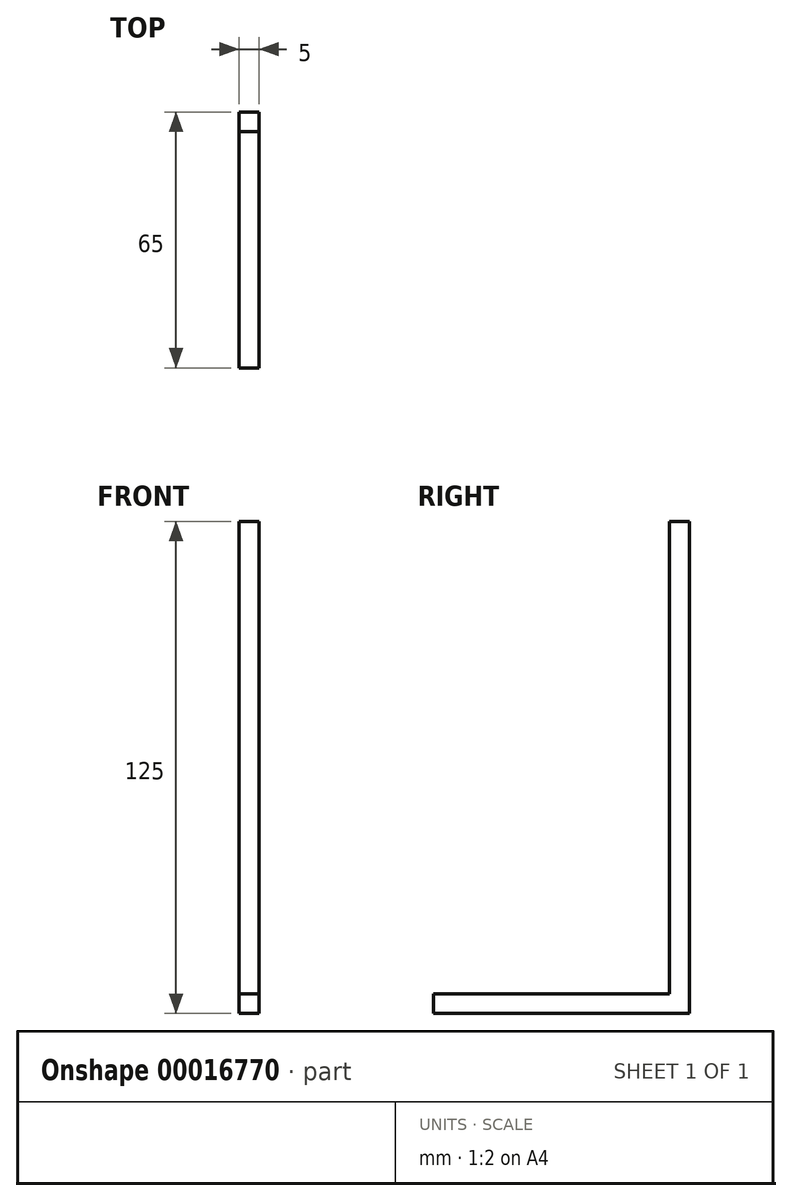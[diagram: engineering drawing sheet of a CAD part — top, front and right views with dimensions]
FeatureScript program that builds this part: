
annotation { "Feature Type Name" : "Feature", "Feature Type Description" : "" }
export const myFeature = defineFeature(function(context is Context, id is Id, definition is map)
    precondition{}
    {
        {
            var Q0;
            Q0=qCreatedBy(makeId("Right.planeOp"),FACE);
            var sketch = newSketch(context, id + "F0", { "sketchPlane" : qUnion([Q0])});
            skLineSegment(sketch, "E0", {"start": v(0, 120) * mm, "end": v(0, 0) * mm});
            skLineSegment(sketch, "E1", {"start": v(0, 0) * mm, "end": v(-60, 0) * mm});
            skLineSegment(sketch, "E2", {"start": v(5, 120) * mm, "end": v(5, -5) * mm});
            skLineSegment(sketch, "E3", {"start": v(-60, -5) * mm, "end": v(5, -5) * mm});
            skLineSegment(sketch, "E4", {"start": v(-60, -5) * mm, "end": v(-60, 0) * mm});
            skLineSegment(sketch, "E5", {"start": v(0, 120) * mm, "end": v(5, 120) * mm});
            skSolve(sketch);
        }
        {
            var Q0;
            Q0=makeQuery(id+"F0.imprint","IMPRINT",FACE,{"disambiguationData":[TD([[makeQuery(id+"F0.imprint","IMPRINT",EDGE,{"derivedFrom":sQuery(id+"F0.wireOp",EDGE,"E0")}),1.0]])]});
            extrude(context, id + "F1", {"entities" : qUnion([Q0]), "depth" : 5 * mm});
        }
    });
